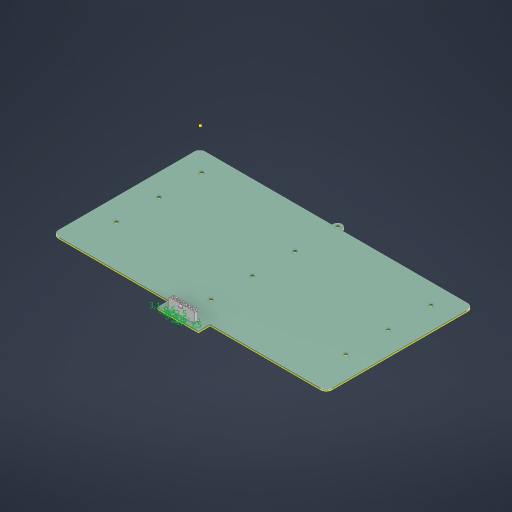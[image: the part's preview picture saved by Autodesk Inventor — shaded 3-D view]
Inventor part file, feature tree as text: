
AUTODESK INVENTOR PART (.ipt)
format: ipt  version: 2024.3 (Build 283343010, 343A)  size: 398,848 bytes
history: native  units: mm
features: sketch x1, projected_geometry x1
ambient origin geometry x8: Origin, YZ Plane, XZ Plane, XY Plane, X Axis, Y Axis, Z Axis, Center Point
bodies: Volumenkörper5 (feature_tree), Volumenkörper34 (feature_tree)
feature tree (2):
  sketch  "Skizze2"  dims[d0=21.5mm d1=3.5mm d2=2.5mm d3=2.5mm d4=0.5mm d5=70.0mm d7=3.0mm d8=10.0mm d10=10.0mm d12=3.1mm d13=2.6mm d14=1.2mm]
  projected_geometry  "Projizierte Kontur1"
